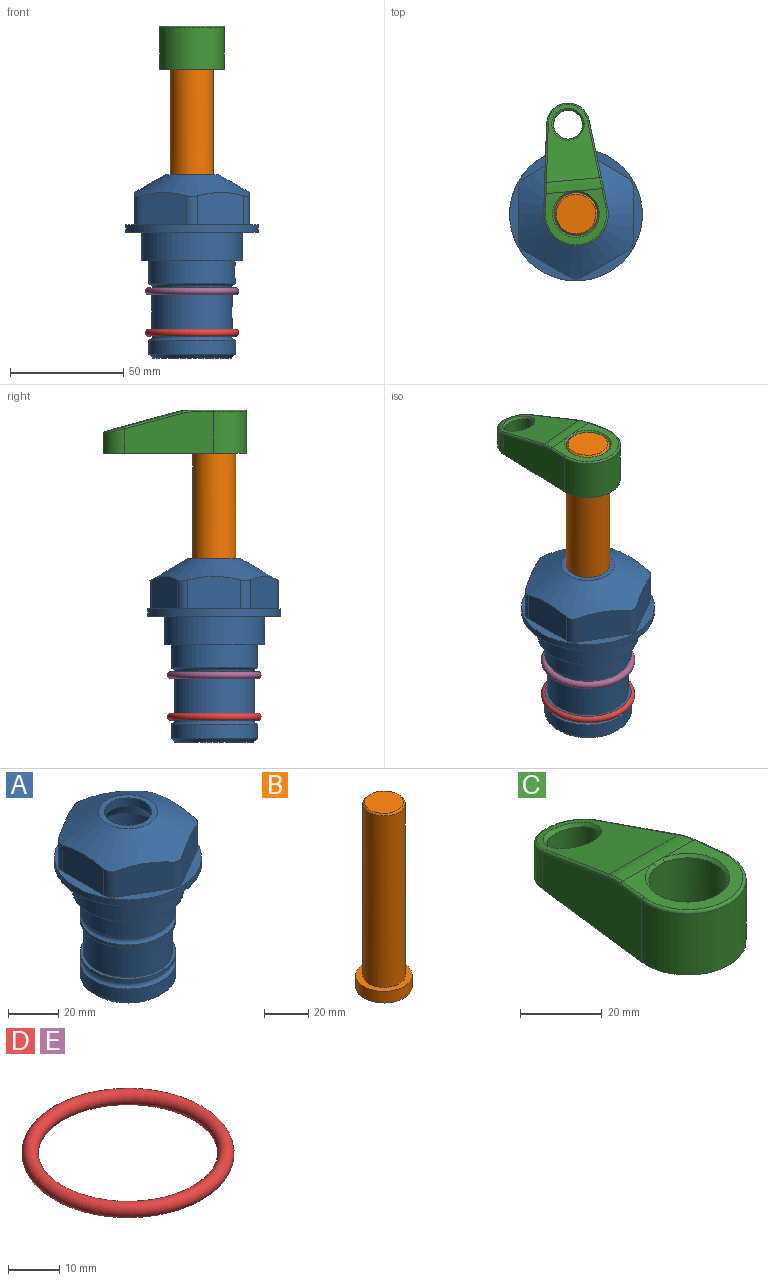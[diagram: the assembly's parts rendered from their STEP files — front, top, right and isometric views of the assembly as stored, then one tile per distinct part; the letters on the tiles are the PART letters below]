
ASSEMBLY  parts=5 mates=4
PART A: 36 faces, bbox 58.7x58.7x81 mm
  f0: cylinder r=17.78mm len=35.56mm, axis (0,0,1), area 1670.8mm2, adj f23,f24,f31
  f1: cylinder r=19.05mm len=38.1mm, axis (0,0,1), area 1191.9mm2, adj f26,f27,f30
  f2: plane 58.66x58.66mm, normal (0,0,-1), area 1150.6mm2, adj f3,f28
  f3: cylinder r=29.33mm len=58.66mm, axis (0,0,-1), area 585.1mm2, adj f2,f4
  f4: plane 58.66x58.66mm, normal (0,0,1), area 475.9mm2, adj f3,f5,f6,f7,f8,f9,f10,f11
  f5: plane 20.32x14.34mm, normal (-0.5,0.87,0), area 324.4mm2, adj f4,f15,f16,f17
  f6: plane 20.32x14.34mm, normal (0.5,0.87,0), area 324.4mm2, adj f4,f14,f15,f17
  f7: plane 23.48x14.34mm, normal (1,0,0), area 324.4mm2, adj f4,f13,f14,f17
  f8: plane 20.32x14.34mm, normal (0.5,-0.87,0), area 324.4mm2, adj f4,f12,f13,f17
  f9: plane 20.32x14.34mm, normal (-0.5,-0.87,0), area 324.4mm2, adj f4,f11,f12,f17
  f10: plane 23.48x14.34mm, normal (-1,0,0), area 324.4mm2, adj f4,f11,f16,f17
  f11: cylinder r=5.08mm len=12.85mm, axis (0,0,-1), area 67.2mm2, adj f4,f9,f10,f17
  f12: cylinder r=5.08mm len=12.85mm, axis (0,0,-1), area 67.2mm2, adj f4,f8,f9,f17
  f13: cylinder r=5.08mm len=12.85mm, axis (0,0,-1), area 67.2mm2, adj f4,f7,f8,f17
  f14: cylinder r=5.08mm len=12.85mm, axis (0,0,-1), area 67.2mm2, adj f4,f6,f7,f17
  f15: cylinder r=5.08mm len=12.85mm, axis (0,0,-1), area 67.2mm2, adj f4,f5,f6,f17
  f16: cylinder r=5.08mm len=12.85mm, axis (0,0,-1), area 67.2mm2, adj f4,f5,f10,f17
  f17: cone r=11.73mm half-angle=60deg, axis (0,0,-1), area 2071.8mm2, adj f5,f6,f7,f8,f9,f10,f11,f12
  f18: plane 23.46x23.46mm, normal (0,0,1), area 147.4mm2, adj f17,f35
  f19: plane 34.93x34.93mm, normal (0,0,-1), area 958mm2, adj f29
  f20: cylinder r=19.05mm len=38.1mm, axis (0,0,1), area 760.1mm2, adj f21,f29
  f21: torus R=19.05mm, axis (0,0,1), area 565.3mm2, adj f20,f22
  f22: cylinder r=19.05mm len=38.1mm, axis (0,0,1), area 190mm2, adj f21,f23
  f23: plane 38.1x38.1mm, normal (0,0,1), area 146.9mm2, adj f0,f22
  f24: plane 38.1x38.1mm, normal (0,0,-1), area 146.9mm2, adj f0,f25
  f25: cylinder r=19.05mm len=38.1mm, axis (0,0,1), area 190mm2, adj f24,f26
  f26: torus R=19.05mm, axis (0,0,1), area 565.3mm2, adj f1,f25
  f27: plane 44.45x44.45mm, normal (0,0,-1), area 411.7mm2, adj f1,f28
  f28: cylinder r=22.23mm len=44.45mm, axis (0,0,1), area 1773.5mm2, adj f2,f27
  f29: cone r=19.05mm half-angle=45deg, axis (0,0,1), area 257.5mm2, adj f19,f20
  f30: cylinder r=3.17mm len=6.75mm, axis (-1,0,0), area 128mm2, adj f1,f33
  f31: cylinder r=3.17mm len=6.35mm, axis (-1,0,0), area 102.5mm2, adj f0,f33
  f32: plane 25.4x25.4mm, normal (0,0,1), area 506.7mm2, adj f33
  f33: cylinder r=12.7mm len=66.42mm, axis (0,0,-1), area 5236.2mm2, adj f30,f31,f32,f34
  f34: cone r=9.53mm half-angle=30deg, axis (0,0,-1), area 443.4mm2, adj f33,f35
  f35: cylinder r=9.53mm len=19.05mm, axis (0,0,-1), area 240.9mm2, adj f18,f34
PART B: 6 faces, bbox 25.4x25.4x101.6 mm
  f0: plane 17.46x17.46mm, normal (0,0,1), area 239.5mm2, adj f5
  f1: plane 25.4x25.4mm, normal (0,0,-1), area 506.7mm2, adj f2
  f2: cylinder r=12.7mm len=25.4mm, axis (0,0,1), area 506.7mm2, adj f1,f3
  f3: plane 25.4x25.4mm, normal (0,0,1), area 221.7mm2, adj f2,f4
  f4: cylinder r=9.53mm len=94.46mm, axis (0,0,1), area 5653mm2, adj f3,f5
  f5: cone r=8.73mm half-angle=45deg, axis (0,0,-1), area 64.4mm2, adj f0,f4
PART C: 31 faces, bbox 31.7x65.5x19.8 mm
  f0: plane 39.12x18.26mm, normal (0.99,0.12,0), area 612.2mm2, adj f1,f4,f7,f11,f13,f15
  f1: cylinder r=9.53mm len=18.91mm, axis (0,0,-1), area 296.1mm2, adj f0,f2,f7,f17
  f2: plane 39.12x18.26mm, normal (-0.99,0.12,0), area 612.2mm2, adj f1,f4,f7,f12,f14,f16
  f3: cylinder r=6.35mm len=12.7mm, axis (0,0,-1), area 362.4mm2, adj f7,f18
  f4: cylinder r=14.29mm len=28.58mm, axis (0,0,-1), area 882.2mm2, adj f0,f2,f7,f10
  f5: cylinder r=9.53mm len=19.05mm, axis (0,0,-1), area 1092.6mm2, adj f7,f19,f20
  f6: plane 26.99x23.69mm, normal (0,0,1), area 216.2mm2, adj f9,f10,f11,f12,f19
  f7: plane 63.5x28.58mm, normal (0,0,-1), area 661.8mm2, adj f0,f1,f2,f3,f4,f5,f22,f23
  f8: plane 33.52x23.6mm, normal (0,0.26,0.97), area 486mm2, adj f9,f15,f16,f17,f18
  f9: cylinder r=19.05mm len=24.72mm, axis (1,0,0), area 120.4mm2, adj f6,f8,f13,f14,f20
  f10: torus R=13.49mm, axis (0,0,1), area 59mm2, adj f4,f6,f11,f12
  f11: cylinder r=0.79mm len=8.67mm, axis (0.12,-0.99,0), area 10.8mm2, adj f0,f6,f10,f13
  f12: cylinder r=0.79mm len=8.67mm, axis (0.12,0.99,0), area 10.8mm2, adj f2,f6,f10,f14
  f13: bspline ~4.95x1.42mm, area 6.1mm2, adj f0,f9,f11,f15
  f14: bspline ~4.95x1.42mm, area 6.1mm2, adj f2,f9,f12,f16
  f15: cylinder r=0.79mm len=25.95mm, axis (0.12,-0.96,0.26), area 32.9mm2, adj f0,f8,f13,f17
  f16: cylinder r=0.79mm len=25.95mm, axis (0.12,0.96,-0.26), area 32.9mm2, adj f2,f8,f14,f17
  f17: bspline ~18.91x8.38mm, area 30mm2, adj f1,f8,f15,f16
  f18: bspline ~14.29x14.29mm, area 48.3mm2, adj f3,f8
  f19: cone r=9.53mm half-angle=45deg, axis (0,0,1), area 66.5mm2, adj f5,f6,f20
  f20: bspline ~3.22x0.96mm, area 3.5mm2, adj f5,f9,f19
  f21: plane 2.75x2.72mm, normal (0,0,-1), area 2.9mm2, adj f23,f25,f28
  f22: plane 23.05x15.88mm, normal (-0.99,-0.12,0), area 323.6mm2, adj f7,f25,f26,f27,f28,f29
  f23: plane 23.05x15.88mm, normal (0.99,-0.12,0), area 323.6mm2, adj f7,f21,f25,f27,f28,f30
  f24: cylinder r=9.53mm len=10.69mm, axis (0,0,-1), area 114.7mm2, adj f7,f27,f29,f30
  f25: cylinder r=12.7mm len=20.59mm, axis (0,0,-1), area 381.1mm2, adj f7,f21,f22,f23,f26,f28
  f26: plane 2.75x2.72mm, normal (0,0,-1), area 2.9mm2, adj f22,f25,f28
  f27: plane 19.72x18.37mm, normal (0,-0.26,-0.97), area 291.8mm2, adj f22,f23,f24,f28,f29,f30
  f28: cylinder r=15.88mm len=19.92mm, axis (1,0,0), area 54.8mm2, adj f21,f22,f23,f25,f26,f27
  f29: cylinder r=1.59mm len=11mm, axis (0,0,-1), area 34.7mm2, adj f7,f22,f24,f27
  f30: cylinder r=1.59mm len=11mm, axis (0,0,-1), area 34.7mm2, adj f7,f23,f24,f27
PART D: 1 faces, bbox 44.7x44.7x3.2 mm
  f0: torus R=19.05mm, axis (0,0,1), area 1193.9mm2
PART E: same geometry as D
PLACE A at identity fixed
PLACE B rot(axis=(0,0,1),5deg) t=(0,0,27.55)mm
PLACE C rot(axis=(0,0,1),5deg) t=(0,0,27.55)mm
PLACE D t=(0,0,-20)mm
PLACE E t=(0,0,-1.59)mm
MATE fastened B.f2 <-> C.f4  axis (0,0,1) through (0,0,91.05)mm
MATE fastened E.f0 <-> A.f0  axis (0,0,1) through (0,0,-26.1)mm
MATE fastened D.f0 <-> A.f0  axis (0,0,1) through (0,0,-44.51)mm
MATE cylindrical B.f2 <-> A.f0  axis (0,0,-1) through (0,0,-10.55)mm
